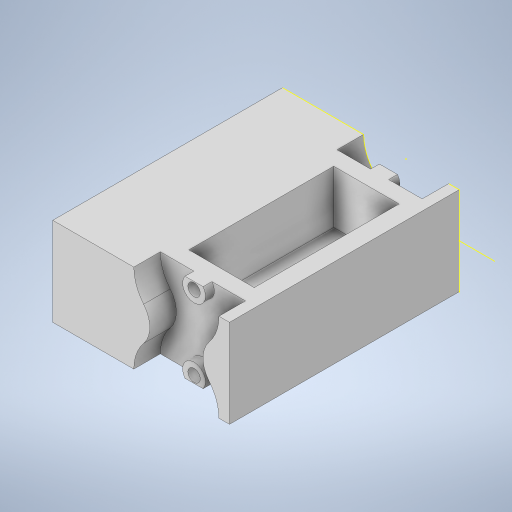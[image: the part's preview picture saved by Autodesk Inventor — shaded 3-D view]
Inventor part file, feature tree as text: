
AUTODESK INVENTOR PART (.ipt)
format: ipt  version: 2024 (Build 280153000, 153)  size: 337,408 bytes
history: native  units: in
note: dims shown in document units (in); Inventor stores cm internally (conversion verified against a paired STEP export)
features: sketch x6, projected_geometry x6, extrude x5, plane x2, mirror x2
ambient origin geometry x8: Origin, YZ Plane, XZ Plane, XY Plane, X Axis, Y Axis, Z Axis, Center Point
bodies: Solid1 (feature_tree)
feature tree (21):
  extrude  "Extrusion1"  Depth=3.937in
  extrude  "Extrusion2"  Depth=3.2283in
  extrude  "Extrusion3"  Depth=0.3937in
  plane  "Work Plane1"
  plane  "Work Plane2"
  extrude  "Extrusion4"  Depth=1.6535in
  mirror  "Mirror1"
  extrude  "Extrusion5"  Depth=0.1575in
  mirror  "Mirror2"
  sketch  "Sketch7"  dims[d12=1.063in d13=0.0in d14=1.1811in d15=2.3661in d16=0.5906in d17=0.0in d18=0.5118in d19=1.6535in d20=0.8268in d21=0.2756in d22=0.1969in d23=0.0in]
  sketch  "Sketch1"  dims[d0=5.1181in d1=3.937in]
  sketch  "Sketch2"  dims[d2=1.9685in d3=0.0in d4=3.2283in]
  projected_geometry  "Projected Loop1"
  sketch  "Sketch3"  dims[d5=1.4567in d6=0.3937in]
  projected_geometry  "Projected Loop2"
  sketch  "Sketch5"  dims[d7=1.1811in d8=0.0in d9=1.6535in]
  projected_geometry  "Projected Loop4"
  sketch  "Sketch6"  dims[d10=3.7402in d11=0.1575in]
  projected_geometry  "Projected Loop5"
  projected_geometry  "Projected Loop6"
  projected_geometry  "Projected Loop7"
